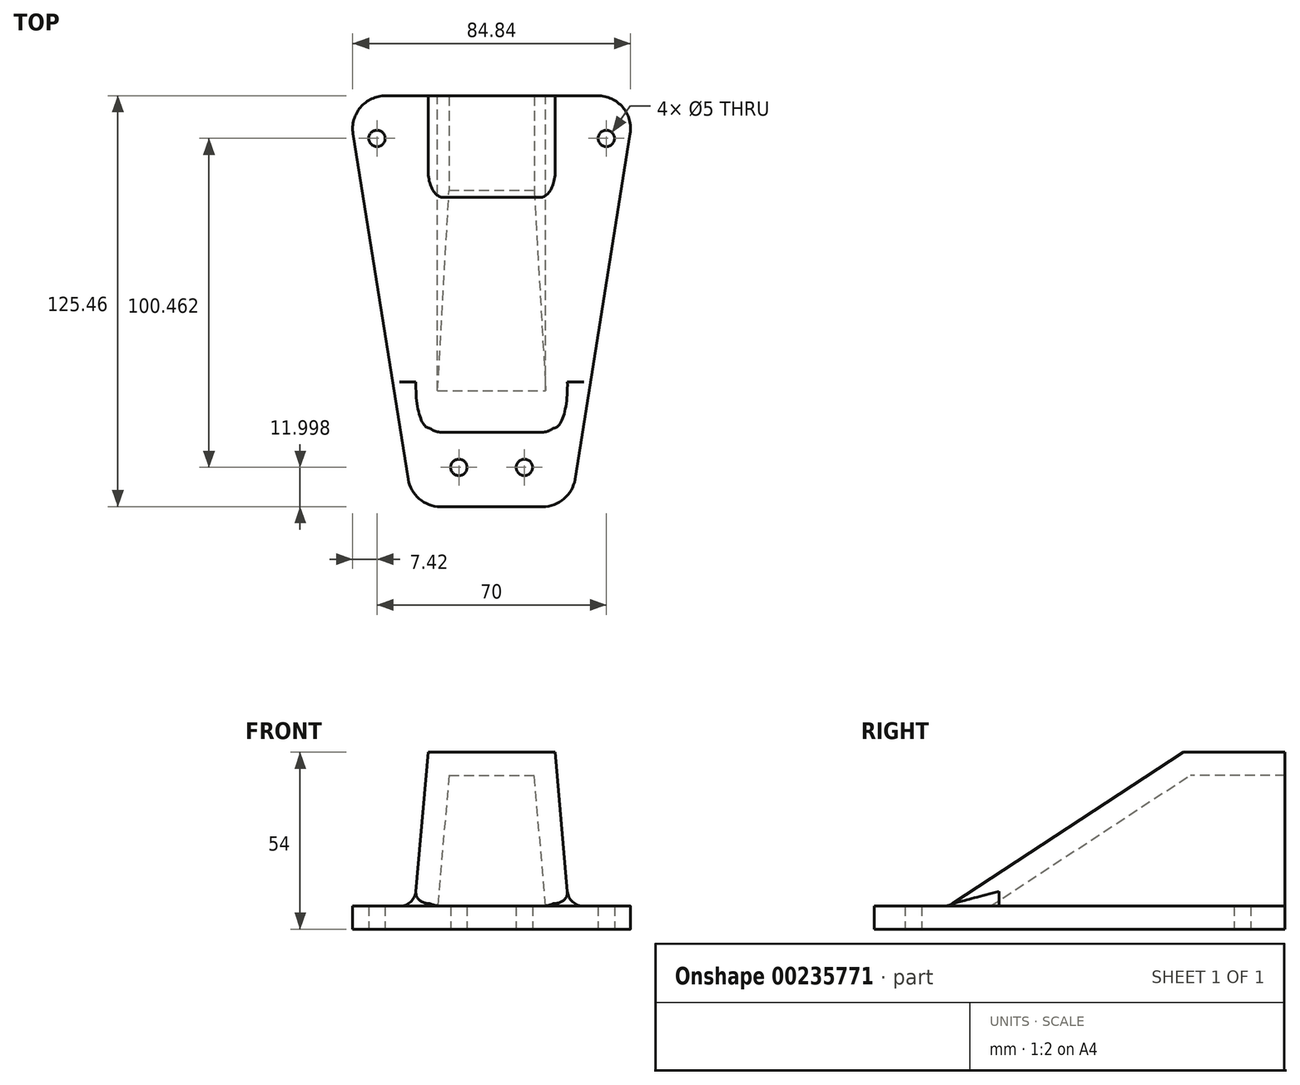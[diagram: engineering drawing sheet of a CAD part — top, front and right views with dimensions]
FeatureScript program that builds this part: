
annotation { "Feature Type Name" : "Feature", "Feature Type Description" : "" }
export const myFeature = defineFeature(function(context is Context, id is Id, definition is map)
    precondition{}
    {
        {
            var Q0;
            Q0=qCreatedBy(makeId("Top.planeOp"),FACE);
            var sketch = newSketch(context, id + "F0", { "sketchPlane" : qUnion([Q0])});
            skLineSegment(sketch, "E0.bottom", {"start": v(0, 0) * mm, "end": v(33, 0) * mm});
            skLineSegment(sketch, "E0.top", {"start": v(0, 90) * mm, "end": v(33, 90) * mm});
            skLineSegment(sketch, "E0.left", {"start": v(0, 0) * mm, "end": v(0, 90) * mm});
            skLineSegment(sketch, "E0.right", {"start": v(33, 0) * mm, "end": v(33, 90) * mm});
            skSolve(sketch);
        }
        {
            var Q0;
            Q0 = qSketchRegion(id + "F0", true);
            extrude(context, id + "F1", {"entities" : qUnion([Q0]), "depth" : 40 * mm});
        }
        {
            var Q0;
            Q0=makeQuery(id+"F1.opExtrude","SWEPT_FACE",FACE,{"disambiguationData":[OSD([sQuery(id+"F0.wireOp",EDGE,"E0.bottom")])]});
            var sketch = newSketch(context, id + "F2", { "sketchPlane" : qUnion([Q0])});
            skLineSegment(sketch, "E1", {"start": v(0, 0) * mm, "end": v(3.5, 40) * mm});
            skLineSegment(sketch, "E2", {"start": v(3.5, 40) * mm, "end": v(29.5, 40) * mm});
            skLineSegment(sketch, "E3", {"start": v(29.5, 40) * mm, "end": v(33, 0) * mm});
            skLineSegment(sketch, "E4", {"start": v(33, 0) * mm, "end": v(67.76, 0) * mm});
            skLineSegment(sketch, "E5", {"start": v(67.76, 0) * mm, "end": v(65.7, 61.44) * mm});
            skLineSegment(sketch, "E6", {"start": v(65.7, 61.44) * mm, "end": v(-18.21, 61.44) * mm});
            skLineSegment(sketch, "E7", {"start": v(-18.21, 61.44) * mm, "end": v(-29.01, 0) * mm});
            skLineSegment(sketch, "E8", {"start": v(-29.01, 0) * mm, "end": v(0, 0) * mm});
            skSolve(sketch);
        }
        {
            var Q0;
            Q0=makeQuery(id+"F1.opExtrude","SWEPT_FACE",FACE,{"disambiguationData":[OSD([sQuery(id+"F0.wireOp",EDGE,"E0.left")])]});
            var sketch = newSketch(context, id + "F3", { "sketchPlane" : qUnion([Q0])});
            skLineSegment(sketch, "E9", {"start": v(0, 0) * mm, "end": v(-61.07, 40) * mm});
            skLineSegment(sketch, "E10", {"start": v(-61.07, 40) * mm, "end": v(-90, 40) * mm});
            skLineSegment(sketch, "E11", {"start": v(-90, 40) * mm, "end": v(-90, 0) * mm});
            skLineSegment(sketch, "E12", {"start": v(-90, 0) * mm, "end": v(-122.19, 0) * mm});
            skLineSegment(sketch, "E13", {"start": v(-122.19, 0) * mm, "end": v(-122.19, 62.63) * mm});
            skLineSegment(sketch, "E14", {"start": v(-122.19, 62.63) * mm, "end": v(27.01, 62.63) * mm});
            skLineSegment(sketch, "E15", {"start": v(27.01, 62.63) * mm, "end": v(27.01, 0) * mm});
            skLineSegment(sketch, "E16", {"start": v(27.01, 0) * mm, "end": v(0, 0) * mm});
            skSolve(sketch);
        }
        {
            var Q0;
            Q0 = qSketchRegion(id + "F3", true);
            extrude(context, id + "F4", {"entities" : qUnion([Q0]), "operationType" : NewBodyOperationType.REMOVE, "oppositeDirection" : true, "depth" : 48.3 * mm});
        }
        {
            var Q0;
            Q0 = qSketchRegion(id + "F2", true);
            extrude(context, id + "F5", {"entities" : qUnion([Q0]), "operationType" : NewBodyOperationType.REMOVE, "endBound" : BoundingType.THROUGH_ALL, "oppositeDirection" : true, "depth" : 90 * mm});
        }
        {
            var Q0;
            Q0=makeQuery(id+"F1.opExtrude","SWEPT_FACE",FACE,{"disambiguationData":[OSD([sQuery(id+"F0.wireOp",EDGE,"E0.top")])]});
            shell(context, id + "F6", {"entities" : qUnion([Q0]), "thickness" : 7 * mm, "oppositeDirection" : true});
        }
        {
            var Q0;
            Q0=makeQuery(id+"F1.opExtrude","CAP_FACE",FACE,{"disambiguationData":[OSD([sQuery(id+"F0.wireOp",EDGE,"E0.bottom"),sQuery(id+"F0.wireOp",EDGE,"E0.top"),sQuery(id+"F0.wireOp",EDGE,"E0.left"),sQuery(id+"F0.wireOp",EDGE,"E0.right")])],"isStart":true});
            var sketch = newSketch(context, id + "F7", { "sketchPlane" : qUnion([Q0])});
            skLineSegment(sketch, "E17.bottom", {"start": v(40.64, 35.46) * mm, "end": v(-7.64, 35.46) * mm});
            skLineSegment(sketch, "E17.top", {"start": v(60.64, -90) * mm, "end": v(-27.64, -90) * mm});
            skLineSegment(sketch, "E18", {"start": v(-27.64, -90) * mm, "end": v(-7.64, 35.46) * mm});
            skLineSegment(sketch, "E19", {"start": v(60.64, -90) * mm, "end": v(40.64, 35.46) * mm});
            skSolve(sketch);
        }
        {
            var Q0;
            Q0 = qSketchRegion(id + "F7", true);
            extrude(context, id + "F8", {"entities" : qUnion([Q0]), "operationType" : NewBodyOperationType.ADD, "oppositeDirection" : true, "depth" : 7 * mm});
        }
        {
            var Q0;
            Q0=makeQuery(id+"F5.boolean.opBoolean","INTERSECT",EDGE,{"derivedFrom":[makeQuery(id+"F4.boolean.opBoolean","COPY",FACE,{"derivedFrom":makeQuery(id+"F4.opExtrude","SWEPT_FACE",FACE,{"disambiguationData":[OSD([sQuery(id+"F3.wireOp",EDGE,"E9")])]})}),makeQuery(id+"F5.opExtrude","SWEPT_FACE",FACE,{"disambiguationData":[OSD([sQuery(id+"F2.wireOp",EDGE,"E1")])]})]});
            var Q1;
            Q1=makeQuery(id+"F5.boolean.opBoolean","INTERSECT",EDGE,{"derivedFrom":[makeQuery(id+"F4.boolean.opBoolean","COPY",FACE,{"derivedFrom":makeQuery(id+"F4.opExtrude","SWEPT_FACE",FACE,{"disambiguationData":[OSD([sQuery(id+"F3.wireOp",EDGE,"E9")])]})}),makeQuery(id+"F5.opExtrude","SWEPT_FACE",FACE,{"disambiguationData":[OSD([sQuery(id+"F2.wireOp",EDGE,"E3")])]})]});
            var Q2;
            Q2=makeQuery(id+"F5.boolean.opBoolean","COPY",EDGE,{"derivedFrom":makeQuery(id+"F5.opExtrude","SWEPT_EDGE",EDGE,{"disambiguationData":[OSD([sQuery(id+"F0.wireOp",EDGE,"E0.bottom"),sQuery(id+"F2.wireOp",EDGE,"E2"),sQuery(id+"F2.wireOp",EDGE,"E3")])]})});
            var Q3;
            Q3=makeQuery(id+"F5.boolean.opBoolean","COPY",EDGE,{"derivedFrom":makeQuery(id+"F5.opExtrude","SWEPT_EDGE",EDGE,{"disambiguationData":[OSD([sQuery(id+"F0.wireOp",EDGE,"E0.bottom"),sQuery(id+"F2.wireOp",EDGE,"E1"),sQuery(id+"F2.wireOp",EDGE,"E2")])]})});
            var Q4;
            Q4=makeQuery(id+"F8.boolean.opBoolean","INTERSECT",EDGE,{"derivedFrom":[makeQuery(id+"F5.boolean.opBoolean","COPY",FACE,{"derivedFrom":makeQuery(id+"F5.opExtrude","SWEPT_FACE",FACE,{"disambiguationData":[OSD([sQuery(id+"F2.wireOp",EDGE,"E1")])]})}),makeQuery(id+"F8.opExtrude","CAP_FACE",FACE,{"disambiguationData":[OSD([sQuery(id+"F7.wireOp",EDGE,"E17.bottom"),sQuery(id+"F7.wireOp",EDGE,"E17.top"),sQuery(id+"F7.wireOp",EDGE,"E17.left"),sQuery(id+"F7.wireOp",EDGE,"E17.right")])],"isStart":false})]});
            var Q5;
            Q5=makeQuery(id+"F8.boolean.opBoolean","INTERSECT",EDGE,{"derivedFrom":[makeQuery(id+"F5.boolean.opBoolean","COPY",FACE,{"derivedFrom":makeQuery(id+"F5.opExtrude","SWEPT_FACE",FACE,{"disambiguationData":[OSD([sQuery(id+"F2.wireOp",EDGE,"E3")])]})}),makeQuery(id+"F8.opExtrude","CAP_FACE",FACE,{"disambiguationData":[OSD([sQuery(id+"F7.wireOp",EDGE,"E17.bottom"),sQuery(id+"F7.wireOp",EDGE,"E17.top"),sQuery(id+"F7.wireOp",EDGE,"E17.left"),sQuery(id+"F7.wireOp",EDGE,"E17.right")])],"isStart":false})]});
            fillet(context, id + "F9", {"entities" : qUnion([Q0, Q1, Q2, Q3, Q4, Q5]), "radius" : 5 * mm, "tangentPropagation" : true, "allowEdgeOverflow" : false});
        }
        {
            var Q0;
            Q0=makeQuery(id+"F8.boolean.opBoolean","MERGE",FACE,{"derivedFrom":[makeQuery(id+"F1.opExtrude","CAP_FACE",FACE,{"disambiguationData":[OSD([sQuery(id+"F0.wireOp",EDGE,"E0.bottom"),sQuery(id+"F0.wireOp",EDGE,"E0.top"),sQuery(id+"F0.wireOp",EDGE,"E0.left"),sQuery(id+"F0.wireOp",EDGE,"E0.right")])],"isStart":true}),makeQuery(id+"F8.opExtrude","CAP_FACE",FACE,{"disambiguationData":[OSD([sQuery(id+"F7.wireOp",EDGE,"E17.bottom"),sQuery(id+"F7.wireOp",EDGE,"E17.top"),sQuery(id+"F7.wireOp",EDGE,"E17.left"),sQuery(id+"F7.wireOp",EDGE,"E17.right")])],"isStart":true})]});
            var sketch = newSketch(context, id + "F10", { "sketchPlane" : qUnion([Q0])});
            skLineSegment(sketch, "E20", {"start": v(16.5, -90) * mm, "end": v(16.5, -108.99) * mm});
            skCircle(sketch, "E21", {"center": v(-18.5, -77) * mm, "radius": 2.5 * mm});
            skCircle(sketch, "E22", {"center": v(6.5, 23.46) * mm, "radius": 2.5 * mm});
            skCircle(sketch, "E23.MirrorC", {"center": v(26.5, 23.46) * mm, "radius": 2.5 * mm});
            skCircle(sketch, "E24.MirrorC", {"center": v(51.5, -77) * mm, "radius": 2.5 * mm});
            skSolve(sketch);
        }
        {
            var Q0;
            Q0 = qSketchRegion(id + "F10", true);
            extrude(context, id + "F11", {"entities" : qUnion([Q0]), "operationType" : NewBodyOperationType.REMOVE, "oppositeDirection" : true, "depth" : 25 * mm});
        }
        {
            var Q0;
            Q0=makeQuery(id+"F8.opExtrude","SWEPT_EDGE",EDGE,{"disambiguationData":[OSD([sQuery(id+"F7.wireOp",EDGE,"E17.top"),sQuery(id+"F7.wireOp",EDGE,"E18")])]});
            var Q1;
            Q1=makeQuery(id+"F8.opExtrude","SWEPT_EDGE",EDGE,{"disambiguationData":[OSD([sQuery(id+"F7.wireOp",EDGE,"E17.top"),sQuery(id+"F7.wireOp",EDGE,"E19")])]});
            var Q2;
            Q2=makeQuery(id+"F8.opExtrude","SWEPT_EDGE",EDGE,{"disambiguationData":[OSD([sQuery(id+"F7.wireOp",EDGE,"E17.bottom"),sQuery(id+"F7.wireOp",EDGE,"E19")])]});
            var Q3;
            Q3=makeQuery(id+"F8.opExtrude","SWEPT_EDGE",EDGE,{"disambiguationData":[OSD([sQuery(id+"F7.wireOp",EDGE,"E17.bottom"),sQuery(id+"F7.wireOp",EDGE,"E18")])]});
            fillet(context, id + "F12", {"entities" : qUnion([Q0, Q1, Q2, Q3]), "radius" : 10 * mm, "tangentPropagation" : true, "allowEdgeOverflow" : false});
        }
    });
